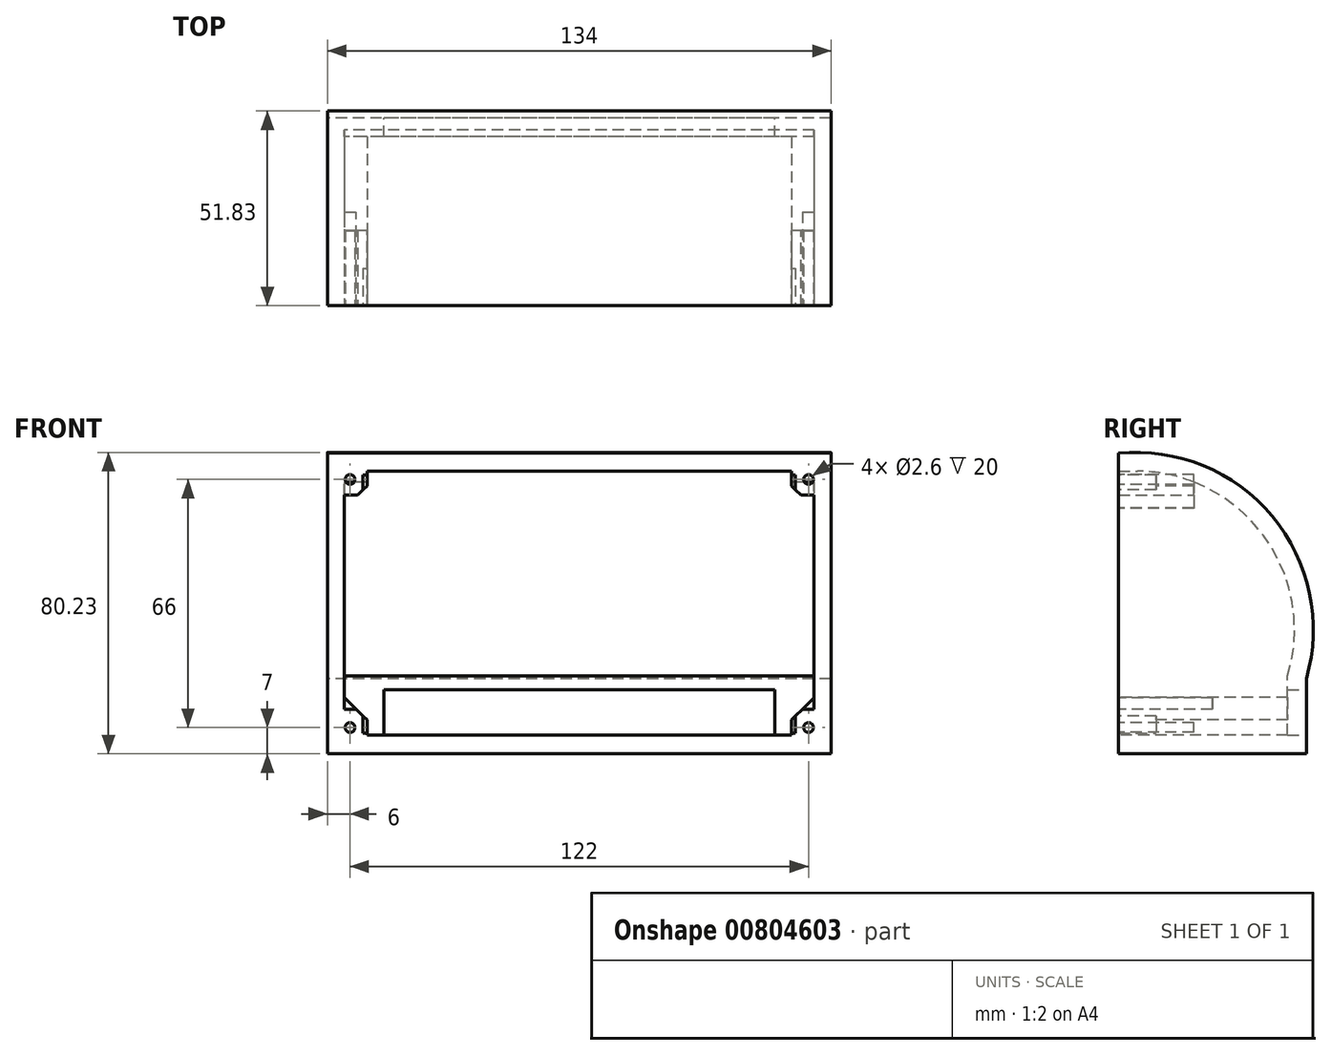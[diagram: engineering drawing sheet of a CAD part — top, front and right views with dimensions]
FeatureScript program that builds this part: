
annotation { "Feature Type Name" : "Feature", "Feature Type Description" : "" }
export const myFeature = defineFeature(function(context is Context, id is Id, definition is map)
    precondition{}
    {
        {
            var Q0;
            Q0=qCreatedBy(makeId("Right.planeOp"),FACE);
            var sketch = newSketch(context, id + "F0", { "sketchPlane" : qUnion([Q0])});
            skLineSegment(sketch, "E0", {"start": v(0, 0) * mm, "end": v(0, 5) * mm});
            skLineSegment(sketch, "E1", {"start": v(0, 0) * mm, "end": v(50, 0) * mm});
            skLineSegment(sketch, "E2", {"start": v(50, 0) * mm, "end": v(50, 20) * mm});
            skArc(sketch, "E3", {"start": v(50, 20) * mm, "mid": v(40.89, 63.24) * mm, "end": v(0, 80) * mm});
            skLineSegment(sketch, "E4.0", {"start": v(45, 5) * mm, "end": v(45, 20.72) * mm});
            skLineSegment(sketch, "E4.1", {"start": v(5, 5) * mm, "end": v(45, 5) * mm});
            skArc(sketch, "E4.3", {"start": v(45, 20.72) * mm, "mid": v(38.65, 57.99) * mm, "end": v(5, 75.22) * mm});
            skLineSegment(sketch, "E5", {"start": v(5, 75.22) * mm, "end": v(0, 75.27) * mm});
            skLineSegment(sketch, "E6", {"start": v(5, 5) * mm, "end": v(0, 5) * mm});
            skLineSegment(sketch, "E7.trimOffspring", {"start": v(0, 75.27) * mm, "end": v(0, 80) * mm});
            skSolve(sketch);
        }
        {
            var Q0;
            Q0=makeQuery(id+"F0.imprint","IMPRINT",FACE,{"disambiguationData":[TD([[makeQuery(id+"F0.imprint","IMPRINT",EDGE,{"derivedFrom":sQuery(id+"F0.wireOp",EDGE,"E0")}),-1.0]])]});
            extrude(context, id + "F1", {"entities" : qUnion([Q0]), "depth" : 125 * mm, "offsetDistance" : 25 * mm});
        }
        {
            var Q0;
            Q0=makeQuery(id+"F1.opExtrude","CAP_FACE",FACE,{"disambiguationData":[OSD([sQuery(id+"F0.wireOp",EDGE,"E0"),sQuery(id+"F0.wireOp",EDGE,"E1"),sQuery(id+"F0.wireOp",EDGE,"E2"),sQuery(id+"F0.wireOp",EDGE,"E3"),sQuery(id+"F0.wireOp",EDGE,"E4.0"),sQuery(id+"F0.wireOp",EDGE,"E4.1"),sQuery(id+"F0.wireOp",EDGE,"E4.3"),sQuery(id+"F0.wireOp",EDGE,"E5"),sQuery(id+"F0.wireOp",EDGE,"E6"),sQuery(id+"F0.wireOp",EDGE,"E7.trimOffspring")])],"isStart":false});
            var sketch = newSketch(context, id + "F2", { "sketchPlane" : qUnion([Q0])});
            skLineSegment(sketch, "E8", {"start": v(0, 75.27) * mm, "end": v(0, 5) * mm});
            skSolve(sketch);
        }
        {
            var Q0;
            Q0=makeQuery(id+"F2.imprint","IMPRINT",FACE,{"disambiguationData":[TD([[makeQuery(id+"F2.imprint","IMPRINT",EDGE,{"derivedFrom":sQuery(id+"F2.wireOp",EDGE,"E8")}),1.0]])]});
            var Q1;
            Q1=makeQuery(id+"F2.imprint","IMPRINT",FACE,{"disambiguationData":[TD([[makeQuery(id+"F2.imprint","IMPRINT",EDGE,{"derivedFrom":makeQuery(id+"F1.opExtrude","CAP_EDGE",EDGE,{"disambiguationData":[OSD([sQuery(id+"F0.wireOp",EDGE,"E0")])],"isStart":false})}),-1.0]])]});
            extrude(context, id + "F3", {"entities" : qUnion([Q0, Q1]), "operationType" : NewBodyOperationType.ADD, "depth" : 4.5 * mm, "offsetDistance" : 25 * mm});
        }
        {
            var Q0;
            Q0=makeQuery(id+"F1.opExtrude","CAP_FACE",FACE,{"disambiguationData":[OSD([sQuery(id+"F0.wireOp",EDGE,"E0"),sQuery(id+"F0.wireOp",EDGE,"E1"),sQuery(id+"F0.wireOp",EDGE,"E2"),sQuery(id+"F0.wireOp",EDGE,"E3"),sQuery(id+"F0.wireOp",EDGE,"E4.0"),sQuery(id+"F0.wireOp",EDGE,"E4.1"),sQuery(id+"F0.wireOp",EDGE,"E4.3"),sQuery(id+"F0.wireOp",EDGE,"E5"),sQuery(id+"F0.wireOp",EDGE,"E6"),sQuery(id+"F0.wireOp",EDGE,"E7.trimOffspring")])],"isStart":true});
            var sketch = newSketch(context, id + "F4", { "sketchPlane" : qUnion([Q0])});
            skLineSegment(sketch, "E9", {"start": v(0, 75.27) * mm, "end": v(0, 5) * mm});
            skSolve(sketch);
        }
        {
            var Q0;
            Q0=makeQuery(id+"F4.imprint","IMPRINT",FACE,{"disambiguationData":[TD([[makeQuery(id+"F4.imprint","IMPRINT",EDGE,{"derivedFrom":sQuery(id+"F4.wireOp",EDGE,"E9")}),-1.0]])]});
            var Q1;
            Q1=makeQuery(id+"F4.imprint","IMPRINT",FACE,{"disambiguationData":[TD([[makeQuery(id+"F4.imprint","IMPRINT",EDGE,{"derivedFrom":makeQuery(id+"F1.opExtrude","CAP_EDGE",EDGE,{"disambiguationData":[OSD([sQuery(id+"F0.wireOp",EDGE,"E0")])],"isStart":true})}),1.0]])]});
            extrude(context, id + "F5", {"entities" : qUnion([Q0, Q1]), "operationType" : NewBodyOperationType.ADD, "depth" : 4.5 * mm, "offsetDistance" : 25 * mm});
        }
        {
            var Q0;
            {var subQ0=sQuery(id+"F0.wireOp",EDGE,"E7.trimOffspring");var subQ1=sQuery(id+"F0.wireOp",EDGE,"E0");Q0=makeQuery(id+"F5.boolean.opBoolean","MERGE",FACE,{"derivedFrom":[makeQuery(id+"F3.boolean.opBoolean","MERGE",FACE,{"derivedFrom":[makeQuery(id+"F1.opExtrude","SWEPT_FACE",FACE,{"disambiguationData":[OSD([subQ1])]}),makeQuery(id+"F1.opExtrude","SWEPT_FACE",FACE,{"disambiguationData":[OSD([subQ0])]}),makeQuery(id+"F3.opExtrude","SWEPT_FACE",FACE,{"disambiguationData":[OSD([subQ1,subQ0,sQuery(id+"F2.wireOp",EDGE,"E8")])]})]}),makeQuery(id+"F5.opExtrude","SWEPT_FACE",FACE,{"disambiguationData":[OSD([subQ1,subQ0,sQuery(id+"F4.wireOp",EDGE,"E9")])]})]});}
            var sketch = newSketch(context, id + "F6", { "sketchPlane" : qUnion([Q0])});
            skLineSegment(sketch, "E10.bottom", {"start": v(0, 75.27) * mm, "end": v(0, 75.27) * mm});
            skLineSegment(sketch, "E11", {"start": v(0, 75.27) * mm, "end": v(0, 65.27) * mm});
            skLineSegment(sketch, "E12", {"start": v(0, 75.27) * mm, "end": v(6, 75.27) * mm});
            skLineSegment(sketch, "E13", {"start": v(6, 71.27) * mm, "end": v(0, 65.27) * mm});
            skLineSegment(sketch, "E14", {"start": v(0, 5) * mm, "end": v(0, 15) * mm});
            skLineSegment(sketch, "E15", {"start": v(0, 5) * mm, "end": v(10, 5) * mm});
            skLineSegment(sketch, "E16", {"start": v(6, 9) * mm, "end": v(0, 15) * mm});
            skLineSegment(sketch, "E17", {"start": v(125, 5) * mm, "end": v(115, 5) * mm});
            skLineSegment(sketch, "E18", {"start": v(125, 5) * mm, "end": v(125, 15) * mm});
            skLineSegment(sketch, "E19", {"start": v(125, 15) * mm, "end": v(119, 9) * mm});
            skLineSegment(sketch, "E20", {"start": v(125, 75.27) * mm, "end": v(119, 75.27) * mm});
            skLineSegment(sketch, "E21", {"start": v(125, 75.27) * mm, "end": v(125, 65.27) * mm});
            skLineSegment(sketch, "E22", {"start": v(125, 65.27) * mm, "end": v(119, 71.27) * mm});
            skLineSegment(sketch, "E23", {"start": v(10, 5) * mm, "end": v(6, 5) * mm});
            skLineSegment(sketch, "E24", {"start": v(6, 5) * mm, "end": v(6, 9) * mm});
            skLineSegment(sketch, "E25", {"start": v(115, 5) * mm, "end": v(119, 5) * mm});
            skLineSegment(sketch, "E26", {"start": v(119, 5) * mm, "end": v(119, 9) * mm});
            skLineSegment(sketch, "E27", {"start": v(6, 75.27) * mm, "end": v(6, 71.27) * mm});
            skLineSegment(sketch, "E28", {"start": v(119, 75.27) * mm, "end": v(119, 71.27) * mm});
            skSolve(sketch);
        }
        {
            var Q0;
            Q0=makeQuery(id+"F6.imprint","IMPRINT",FACE,{"disambiguationData":[TD([[makeQuery(id+"F6.imprint","IMPRINT",EDGE,{"derivedFrom":sQuery(id+"F6.wireOp",EDGE,"E14")}),1.0]])]});
            var Q1;
            Q1=makeQuery(id+"F6.imprint","IMPRINT",FACE,{"disambiguationData":[TD([[makeQuery(id+"F6.imprint","IMPRINT",EDGE,{"derivedFrom":sQuery(id+"F6.wireOp",EDGE,"E17")}),-1.0]])]});
            extrude(context, id + "F7", {"entities" : qUnion([Q0, Q1]), "operationType" : NewBodyOperationType.ADD, "oppositeDirection" : true, "depth" : 45 * mm, "offsetDistance" : 25 * mm});
        }
        {
            var Q0;
            {var subQ0=sQuery(id+"F0.wireOp",EDGE,"E7.trimOffspring");var subQ1=sQuery(id+"F0.wireOp",EDGE,"E0");Q0=makeQuery(id+"F7.boolean.opBoolean","MERGE",FACE,{"derivedFrom":[makeQuery(id+"F5.boolean.opBoolean","MERGE",FACE,{"derivedFrom":[makeQuery(id+"F3.boolean.opBoolean","MERGE",FACE,{"derivedFrom":[makeQuery(id+"F1.opExtrude","SWEPT_FACE",FACE,{"disambiguationData":[OSD([subQ1])]}),makeQuery(id+"F1.opExtrude","SWEPT_FACE",FACE,{"disambiguationData":[OSD([subQ0])]}),makeQuery(id+"F3.opExtrude","SWEPT_FACE",FACE,{"disambiguationData":[OSD([subQ1,subQ0,sQuery(id+"F2.wireOp",EDGE,"E8")])]})]}),makeQuery(id+"F5.opExtrude","SWEPT_FACE",FACE,{"disambiguationData":[OSD([subQ1,subQ0,sQuery(id+"F4.wireOp",EDGE,"E9")])]})]}),makeQuery(id+"F7.opExtrude","CAP_FACE",FACE,{"disambiguationData":[OSD([sQuery(id+"F6.wireOp",EDGE,"E14"),sQuery(id+"F6.wireOp",EDGE,"E15"),sQuery(id+"F6.wireOp",EDGE,"E16")])],"isStart":true}),makeQuery(id+"F7.opExtrude","CAP_FACE",FACE,{"disambiguationData":[OSD([sQuery(id+"F6.wireOp",EDGE,"E17"),sQuery(id+"F6.wireOp",EDGE,"E18"),sQuery(id+"F6.wireOp",EDGE,"E19")])],"isStart":true})]});}
            var sketch = newSketch(context, id + "F8", { "sketchPlane" : qUnion([Q0])});
            skLineSegment(sketch, "E29", {"start": v(0, 75.27) * mm, "end": v(0, 65.27) * mm});
            skLineSegment(sketch, "E30", {"start": v(0, 75.27) * mm, "end": v(10, 75.27) * mm});
            skLineSegment(sketch, "E31", {"start": v(6, 71.27) * mm, "end": v(0, 65.27) * mm});
            skLineSegment(sketch, "E32", {"start": v(125, 75.27) * mm, "end": v(115, 75.27) * mm});
            skLineSegment(sketch, "E33", {"start": v(125, 75.27) * mm, "end": v(125, 65.27) * mm});
            skLineSegment(sketch, "E34", {"start": v(125, 65.27) * mm, "end": v(119, 71.27) * mm});
            skLineSegment(sketch, "E35", {"start": v(0, 75.27) * mm, "end": v(4.02, 75.27) * mm});
            skLineSegment(sketch, "E36", {"start": v(10, 75.27) * mm, "end": v(6, 75.27) * mm});
            skLineSegment(sketch, "E37", {"start": v(6, 75.27) * mm, "end": v(6, 71.27) * mm});
            skLineSegment(sketch, "E38", {"start": v(115, 75.27) * mm, "end": v(119, 75.27) * mm});
            skLineSegment(sketch, "E39", {"start": v(119, 75.27) * mm, "end": v(119, 71.27) * mm});
            skSolve(sketch);
        }
        {
            var Q0;
            Q0=makeQuery(id+"F8.imprint","IMPRINT",FACE,{"disambiguationData":[TD([[makeQuery(id+"F8.imprint","IMPRINT",EDGE,{"derivedFrom":sQuery(id+"F8.wireOp",EDGE,"E29")}),1.0]])]});
            var Q1;
            Q1=makeQuery(id+"F8.imprint","IMPRINT",FACE,{"disambiguationData":[TD([[makeQuery(id+"F8.imprint","IMPRINT",EDGE,{"derivedFrom":sQuery(id+"F8.wireOp",EDGE,"E32")}),1.0]])]});
            extrude(context, id + "F9", {"entities" : qUnion([Q0, Q1]), "operationType" : NewBodyOperationType.ADD, "oppositeDirection" : true, "depth" : 20 * mm, "offsetDistance" : 25 * mm});
        }
        {
            var Q0;
            {var subQ0=sQuery(id+"F0.wireOp",EDGE,"E7.trimOffspring");var subQ1=sQuery(id+"F0.wireOp",EDGE,"E0");Q0=makeQuery(id+"F9.boolean.opBoolean","MERGE",FACE,{"derivedFrom":[makeQuery(id+"F7.boolean.opBoolean","MERGE",FACE,{"derivedFrom":[makeQuery(id+"F5.boolean.opBoolean","MERGE",FACE,{"derivedFrom":[makeQuery(id+"F3.boolean.opBoolean","MERGE",FACE,{"derivedFrom":[makeQuery(id+"F1.opExtrude","SWEPT_FACE",FACE,{"disambiguationData":[OSD([subQ1])]}),makeQuery(id+"F1.opExtrude","SWEPT_FACE",FACE,{"disambiguationData":[OSD([subQ0])]}),makeQuery(id+"F3.opExtrude","SWEPT_FACE",FACE,{"disambiguationData":[OSD([subQ1,subQ0,sQuery(id+"F2.wireOp",EDGE,"E8")])]})]}),makeQuery(id+"F5.opExtrude","SWEPT_FACE",FACE,{"disambiguationData":[OSD([subQ1,subQ0,sQuery(id+"F4.wireOp",EDGE,"E9")])]})]}),makeQuery(id+"F7.opExtrude","CAP_FACE",FACE,{"disambiguationData":[OSD([sQuery(id+"F6.wireOp",EDGE,"E14"),sQuery(id+"F6.wireOp",EDGE,"E15"),sQuery(id+"F6.wireOp",EDGE,"E16")])],"isStart":true}),makeQuery(id+"F7.opExtrude","CAP_FACE",FACE,{"disambiguationData":[OSD([sQuery(id+"F6.wireOp",EDGE,"E17"),sQuery(id+"F6.wireOp",EDGE,"E18"),sQuery(id+"F6.wireOp",EDGE,"E19")])],"isStart":true})]}),makeQuery(id+"F9.opExtrude","CAP_FACE",FACE,{"disambiguationData":[OSD([sQuery(id+"F8.wireOp",EDGE,"E29"),sQuery(id+"F8.wireOp",EDGE,"E30"),sQuery(id+"F8.wireOp",EDGE,"E31")])],"isStart":true}),makeQuery(id+"F9.opExtrude","CAP_FACE",FACE,{"disambiguationData":[OSD([sQuery(id+"F8.wireOp",EDGE,"E32"),sQuery(id+"F8.wireOp",EDGE,"E33"),sQuery(id+"F8.wireOp",EDGE,"E34")])],"isStart":true})]});}
            var sketch = newSketch(context, id + "F10", { "sketchPlane" : qUnion([Q0])});
            skCircle(sketch, "E40", {"center": v(1.5, 73) * mm, "radius": 1.3 * mm});
            skCircle(sketch, "E41", {"center": v(123.5, 73) * mm, "radius": 1.3 * mm});
            skCircle(sketch, "E42", {"center": v(123.5, 7) * mm, "radius": 1.3 * mm});
            skCircle(sketch, "E43", {"center": v(1.5, 7) * mm, "radius": 1.3 * mm});
            skPoint(sketch, "E44.endSnap0", {"position": v(122, 68.27) * mm});
            skLineSegment(sketch, "E45", {"start": v(1.5, 73) * mm, "end": v(-4.5, 73) * mm});
            skLineSegment(sketch, "E46", {"start": v(1.5, 7) * mm, "end": v(-4.5, 7) * mm});
            skLineSegment(sketch, "E47", {"start": v(129.5, 7) * mm, "end": v(123.5, 7) * mm});
            skLineSegment(sketch, "E48", {"start": v(129.5, 73) * mm, "end": v(123.5, 73) * mm});
            skSolve(sketch);
        }
        {
            var Q0;
            Q0 = qSketchRegion(id + "F10", true);
            extrude(context, id + "F11", {"entities" : qUnion([Q0]), "operationType" : NewBodyOperationType.REMOVE, "oppositeDirection" : true, "depth" : 20 * mm, "offsetDistance" : 25 * mm});
        }
        {
            var Q0;
            {var subQ0=sQuery(id+"F0.wireOp",EDGE,"E7.trimOffspring");var subQ1=sQuery(id+"F0.wireOp",EDGE,"E0");Q0=makeQuery(id+"F9.boolean.opBoolean","MERGE",FACE,{"derivedFrom":[makeQuery(id+"F7.boolean.opBoolean","MERGE",FACE,{"derivedFrom":[makeQuery(id+"F5.boolean.opBoolean","MERGE",FACE,{"derivedFrom":[makeQuery(id+"F3.boolean.opBoolean","MERGE",FACE,{"derivedFrom":[makeQuery(id+"F1.opExtrude","SWEPT_FACE",FACE,{"disambiguationData":[OSD([subQ1])]}),makeQuery(id+"F1.opExtrude","SWEPT_FACE",FACE,{"disambiguationData":[OSD([subQ0])]}),makeQuery(id+"F3.opExtrude","SWEPT_FACE",FACE,{"disambiguationData":[OSD([subQ1,subQ0,sQuery(id+"F2.wireOp",EDGE,"E8")])]})]}),makeQuery(id+"F5.opExtrude","SWEPT_FACE",FACE,{"disambiguationData":[OSD([subQ1,subQ0,sQuery(id+"F4.wireOp",EDGE,"E9")])]})]}),makeQuery(id+"F7.opExtrude","CAP_FACE",FACE,{"disambiguationData":[OSD([sQuery(id+"F6.wireOp",EDGE,"E14"),sQuery(id+"F6.wireOp",EDGE,"E15"),sQuery(id+"F6.wireOp",EDGE,"E16"),sQuery(id+"F6.wireOp",EDGE,"E24")])],"isStart":true}),makeQuery(id+"F7.opExtrude","CAP_FACE",FACE,{"disambiguationData":[OSD([sQuery(id+"F6.wireOp",EDGE,"E17"),sQuery(id+"F6.wireOp",EDGE,"E18"),sQuery(id+"F6.wireOp",EDGE,"E19"),sQuery(id+"F6.wireOp",EDGE,"E26")])],"isStart":true})]}),makeQuery(id+"F9.opExtrude","CAP_FACE",FACE,{"disambiguationData":[OSD([sQuery(id+"F8.wireOp",EDGE,"E29"),sQuery(id+"F8.wireOp",EDGE,"E30"),sQuery(id+"F8.wireOp",EDGE,"E31")])],"isStart":true}),makeQuery(id+"F9.opExtrude","CAP_FACE",FACE,{"disambiguationData":[OSD([sQuery(id+"F8.wireOp",EDGE,"E32"),sQuery(id+"F8.wireOp",EDGE,"E33"),sQuery(id+"F8.wireOp",EDGE,"E34")])],"isStart":true})]});}
            var sketch = newSketch(context, id + "F12", { "sketchPlane" : qUnion([Q0])});
            skSolve(sketch);
        }
        {
            var Q0;
            {var subQ0=sQuery(id+"F0.wireOp",EDGE,"E2");Q0=makeQuery(id+"F5.boolean.opBoolean","MERGE",FACE,{"derivedFrom":[makeQuery(id+"F3.boolean.opBoolean","MERGE",FACE,{"derivedFrom":[makeQuery(id+"F1.opExtrude","SWEPT_FACE",FACE,{"disambiguationData":[OSD([subQ0])]}),makeQuery(id+"F3.opExtrude","SWEPT_FACE",FACE,{"disambiguationData":[OSD([subQ0])]})]}),makeQuery(id+"F5.opExtrude","SWEPT_FACE",FACE,{"disambiguationData":[OSD([subQ0])]})]});}
            var sketch = newSketch(context, id + "F13", { "sketchPlane" : qUnion([Q0])});
            skLineSegment(sketch, "E49.0", {"start": v(-114.5, 17) * mm, "end": v(-10.5, 17) * mm});
            skLineSegment(sketch, "E50.0", {"start": v(-114.5, 5) * mm, "end": v(-10.5, 5) * mm});
            skLineSegment(sketch, "E51.0", {"start": v(-114.5, 5) * mm, "end": v(-114.5, 17) * mm});
            skLineSegment(sketch, "E52.0", {"start": v(-10.5, 5) * mm, "end": v(-10.5, 17) * mm});
            skSolve(sketch);
        }
        {
            var Q0;
            Q0=makeQuery(id+"F13.imprint","IMPRINT",FACE,{"disambiguationData":[TD([[makeQuery(id+"F13.imprint","IMPRINT",EDGE,{"derivedFrom":sQuery(id+"F13.wireOp",EDGE,"E49.0")}),-1.0]])]});
            extrude(context, id + "F14", {"entities" : qUnion([Q0]), "operationType" : NewBodyOperationType.REMOVE, "oppositeDirection" : true, "depth" : 5 * mm, "offsetDistance" : 25 * mm});
        }
        {
            var Q0;
            Q0=makeQuery(id+"F12.imprint","IMPRINT",FACE,{"disambiguationData":[TD([[makeQuery(id+"F12.imprint","IMPRINT",EDGE,{"derivedFrom":makeQuery(id+"F7.opExtrude","CAP_EDGE",EDGE,{"disambiguationData":[OSD([sQuery(id+"F6.wireOp",EDGE,"E16")])],"isStart":true})}),1.0]])]});
            var sketch = newSketch(context, id + "F15", { "sketchPlane" : qUnion([Q0])});
            skLineSegment(sketch, "E53.bottom", {"start": v(4.94, 74.23) * mm, "end": v(120.03, 74.23) * mm});
            skLineSegment(sketch, "E53.top", {"start": v(4.94, 5.44) * mm, "end": v(120.03, 5.44) * mm});
            skLineSegment(sketch, "E53.left", {"start": v(4.94, 74.23) * mm, "end": v(4.94, 5.44) * mm});
            skLineSegment(sketch, "E53.right", {"start": v(120.03, 74.23) * mm, "end": v(120.03, 5.44) * mm});
            skSolve(sketch);
        }
        {
            var Q0;
            Q0 = qSketchRegion(id + "F15", true);
            extrude(context, id + "F16", {"entities" : qUnion([Q0]), "operationType" : NewBodyOperationType.REMOVE, "oppositeDirection" : true, "depth" : 10 * mm, "offsetDistance" : 25 * mm});
        }
        {
            var Q0;
            Q0=makeQuery(id+"F12.imprint","IMPRINT",FACE,{"disambiguationData":[TD([[makeQuery(id+"F12.imprint","IMPRINT",EDGE,{"derivedFrom":makeQuery(id+"F7.opExtrude","CAP_EDGE",EDGE,{"disambiguationData":[OSD([sQuery(id+"F6.wireOp",EDGE,"E16")])],"isStart":true})}),1.0]])]});
            var sketch = newSketch(context, id + "F17", { "sketchPlane" : qUnion([Q0])});
            skLineSegment(sketch, "E54.bottom", {"start": v(0, 68.8) * mm, "end": v(124.87, 68.8) * mm});
            skLineSegment(sketch, "E54.top", {"start": v(0, 11.9) * mm, "end": v(124.87, 11.9) * mm});
            skLineSegment(sketch, "E54.left", {"start": v(0, 68.8) * mm, "end": v(0, 11.9) * mm});
            skLineSegment(sketch, "E54.right", {"start": v(124.87, 68.8) * mm, "end": v(124.87, 11.9) * mm});
            skSolve(sketch);
        }
        {
            var Q0;
            Q0 = qSketchRegion(id + "F17", true);
            extrude(context, id + "F18", {"entities" : qUnion([Q0]), "operationType" : NewBodyOperationType.REMOVE, "oppositeDirection" : true, "depth" : 25 * mm, "offsetDistance" : 25 * mm});
        }
    });
